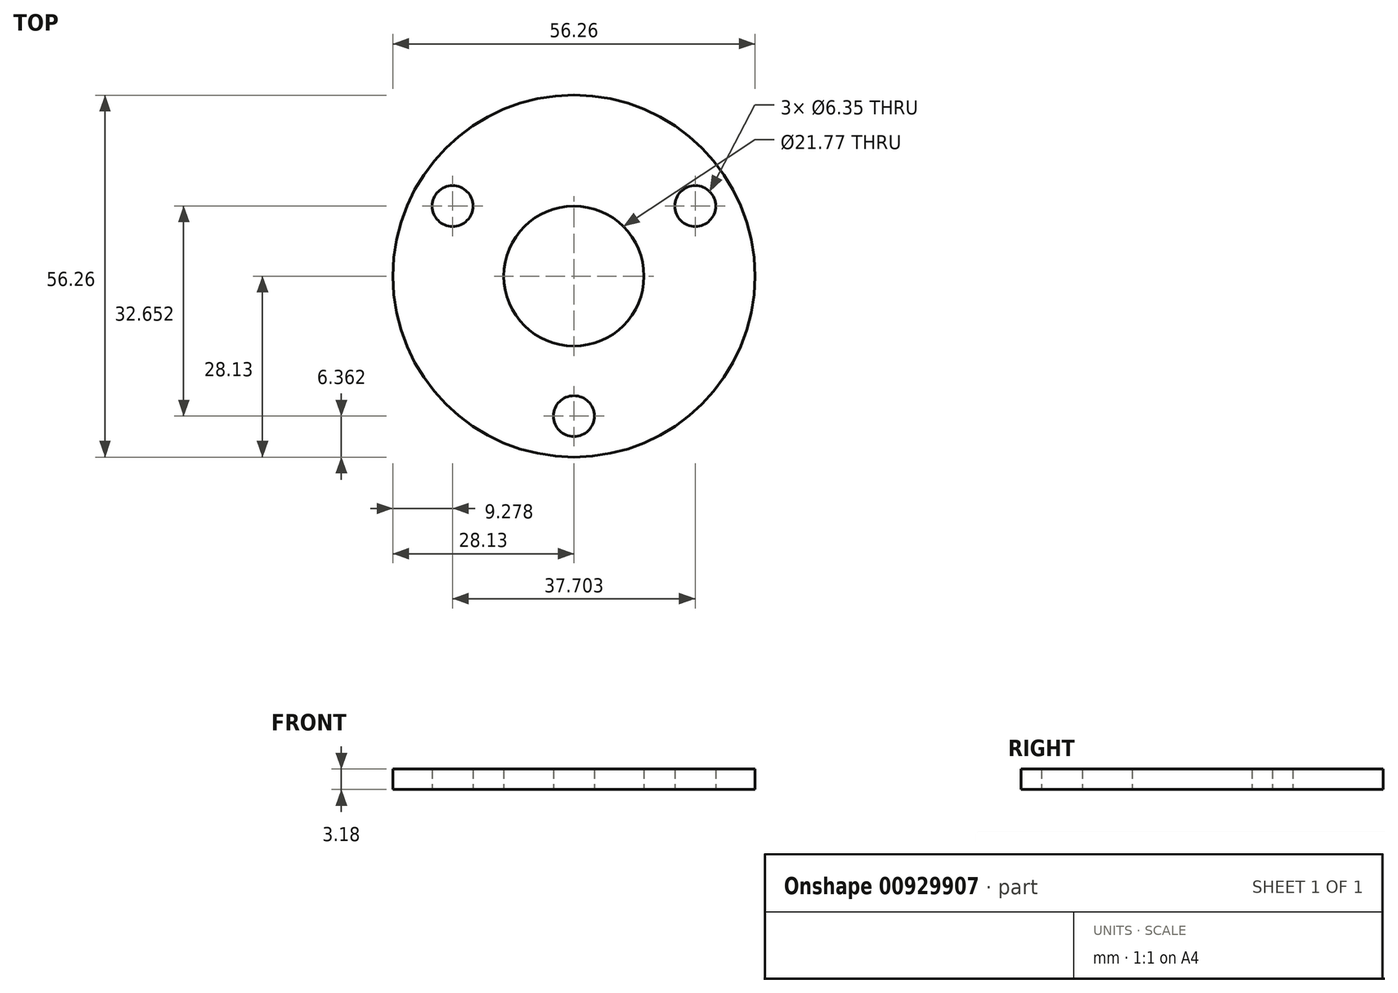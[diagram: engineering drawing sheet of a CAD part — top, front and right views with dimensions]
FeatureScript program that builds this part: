
annotation { "Feature Type Name" : "Feature", "Feature Type Description" : "" }
export const myFeature = defineFeature(function(context is Context, id is Id, definition is map)
    precondition{}
    {
        {
            var Q0;
            Q0=qCreatedBy(makeId("Top.planeOp"),FACE);
            var sketch = newSketch(context, id + "F0", { "sketchPlane" : qUnion([Q0])});
            skCircle(sketch, "E0", {"center": v(0, 0) * mm, "radius": 10.88 * mm});
            skCircle(sketch, "E1.cCircle", {"center": v(0, 0) * mm, "radius": 10.88 * mm, "construction": true});
            skLineSegment(sketch, "E1.0", {"start": v(-18.85, 10.88) * mm, "end": v(18.85, 10.88) * mm});
            skLineSegment(sketch, "E1.1", {"start": v(18.85, 10.88) * mm, "end": v(0, -21.77) * mm});
            skLineSegment(sketch, "E1.2", {"start": v(0, -21.77) * mm, "end": v(-18.85, 10.88) * mm});
            skPoint(sketch, "E1.0.midPoint", {"position": v(0, 10.88) * mm});
            skCircle(sketch, "E2", {"center": v(0, 0) * mm, "radius": 28.13 * mm});
            skCircle(sketch, "E3", {"center": v(-18.85, 10.88) * mm, "radius": 3.18 * mm});
            skCircle(sketch, "E4", {"center": v(18.85, 10.88) * mm, "radius": 3.18 * mm});
            skCircle(sketch, "E5", {"center": v(0, -21.77) * mm, "radius": 3.18 * mm});
            skCircle(sketch, "E6", {"center": v(0, 0) * mm, "radius": 7.94 * mm});
            skSolve(sketch);
        }
        {
            var Q0;
            Q0=makeQuery(id+"F0.imprint","IMPRINT",FACE,{"disambiguationData":[TD([[makeQuery(id+"F0.imprint","IMPRINT",EDGE,{"derivedFrom":sQuery(id+"F0.wireOp",EDGE,"E2")}),1.0]])]});
            var Q1;
            {var subQ0=sQuery(id+"F0.wireOp",EDGE,"E1.0");var subQ1=sQuery(id+"F0.wireOp",EDGE,"E0");var subQ2=makeQuery(id+"F0.imprint","INTERSECT",VERTEX,{"derivedFrom":[subQ1,subQ0]});Q1=makeQuery(id+"F0.imprint","IMPRINT",FACE,{"disambiguationData":[TD([[makeQuery(id+"F0.imprint","IMPRINT",EDGE,{"disambiguationData":[TD([[subQ2,1.0]])],"derivedFrom":subQ1}),-1.0]])]});}
            var Q2;
            {var subQ0=sQuery(id+"F0.wireOp",EDGE,"E1.2");var subQ1=sQuery(id+"F0.wireOp",EDGE,"E0");var subQ2=makeQuery(id+"F0.imprint","INTERSECT",VERTEX,{"derivedFrom":[subQ1,subQ0]});Q2=makeQuery(id+"F0.imprint","IMPRINT",FACE,{"disambiguationData":[TD([[makeQuery(id+"F0.imprint","IMPRINT",EDGE,{"disambiguationData":[TD([[subQ2,1.0]])],"derivedFrom":subQ1}),-1.0]])]});}
            var Q3;
            {var subQ0=sQuery(id+"F0.wireOp",EDGE,"E1.2");var subQ1=sQuery(id+"F0.wireOp",EDGE,"E0");var subQ2=makeQuery(id+"F0.imprint","INTERSECT",VERTEX,{"derivedFrom":[subQ1,subQ0]});Q3=makeQuery(id+"F0.imprint","IMPRINT",FACE,{"disambiguationData":[TD([[makeQuery(id+"F0.imprint","IMPRINT",EDGE,{"disambiguationData":[TD([[subQ2,-1.0]])],"derivedFrom":subQ1}),-1.0]])]});}
            extrude(context, id + "F1", {"entities" : qUnion([Q0, Q1, Q2, Q3]), "endBound" : BoundingType.SYMMETRIC, "depth" : 3.17 * mm, "offsetDistance" : 25.4 * mm});
        }
    });
